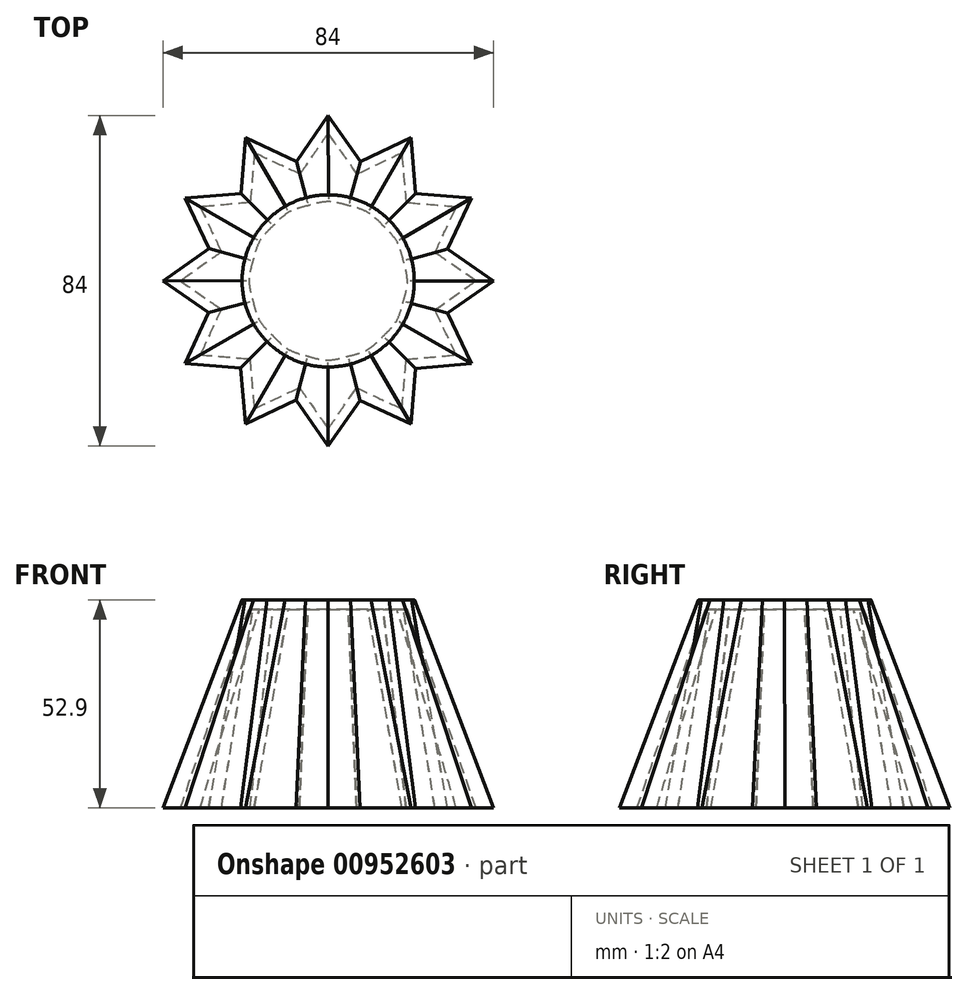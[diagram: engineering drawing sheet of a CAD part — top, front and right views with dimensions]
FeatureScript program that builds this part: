
annotation { "Feature Type Name" : "Feature", "Feature Type Description" : "" }
export const myFeature = defineFeature(function(context is Context, id is Id, definition is map)
    precondition{}
    {
        {
            var Q0;
            Q0=qCreatedBy(makeId("Top.planeOp"),FACE);
            cPlane(context, id + "F0", {"entities" : qUnion([Q0]), "cplaneType" : CPlaneType.OFFSET, "offset" : 47 * mm, "width" : 150 * mm, "height" : 150 * mm});
        }
        {
            var Q0;
            Q0=qCreatedBy(id+"F0.planeOp",FACE);
            var sketch = newSketch(context, id + "F1", { "sketchPlane" : qUnion([Q0])});
            skLineSegment(sketch, "E0", {"start": v(-9.31, 28.52) * mm, "end": v(0, 42) * mm});
            skLineSegment(sketch, "E1", {"start": v(0, 42) * mm, "end": v(9.47, 28.47) * mm});
            skLineSegment(sketch, "E2.1.0", {"start": v(-22.33, 20.04) * mm, "end": v(-21, 36.37) * mm});
            skLineSegment(sketch, "E2.2.0", {"start": v(-29.35, 6.2) * mm, "end": v(-36.37, 21) * mm});
            skLineSegment(sketch, "E2.3.0", {"start": v(-28.52, -9.31) * mm, "end": v(-42, 0) * mm});
            skLineSegment(sketch, "E2.4.0", {"start": v(-20.04, -22.33) * mm, "end": v(-36.37, -21) * mm});
            skLineSegment(sketch, "E2.5.0", {"start": v(-6.2, -29.35) * mm, "end": v(-21, -36.37) * mm});
            skLineSegment(sketch, "E2.6.0", {"start": v(9.31, -28.52) * mm, "end": v(0, -42) * mm});
            skLineSegment(sketch, "E2.7.0", {"start": v(22.33, -20.04) * mm, "end": v(21, -36.37) * mm});
            skLineSegment(sketch, "E2.8.0", {"start": v(29.35, -6.2) * mm, "end": v(36.37, -21) * mm});
            skLineSegment(sketch, "E2.9.0", {"start": v(28.52, 9.31) * mm, "end": v(42, 0) * mm});
            skLineSegment(sketch, "E2.10.0", {"start": v(20.04, 22.33) * mm, "end": v(36.37, 21) * mm});
            skLineSegment(sketch, "E2.11.0", {"start": v(6.2, 29.35) * mm, "end": v(21, 36.37) * mm});
            skPoint(sketch, "E2.center", {"position": v(0, 0) * mm});
            skLineSegment(sketch, "E3.1.0", {"start": v(-21, 36.37) * mm, "end": v(-6.03, 29.39) * mm});
            skLineSegment(sketch, "E3.2.0", {"start": v(-36.37, 21) * mm, "end": v(-19.92, 22.44) * mm});
            skLineSegment(sketch, "E3.3.0", {"start": v(-42, 0) * mm, "end": v(-28.47, 9.47) * mm});
            skLineSegment(sketch, "E3.4.0", {"start": v(-36.37, -21) * mm, "end": v(-29.39, -6.03) * mm});
            skLineSegment(sketch, "E3.5.0", {"start": v(-21, -36.37) * mm, "end": v(-22.44, -19.92) * mm});
            skLineSegment(sketch, "E3.6.0", {"start": v(0, -42) * mm, "end": v(-9.47, -28.47) * mm});
            skLineSegment(sketch, "E3.7.0", {"start": v(21, -36.37) * mm, "end": v(6.03, -29.39) * mm});
            skLineSegment(sketch, "E3.8.0", {"start": v(36.37, -21) * mm, "end": v(19.92, -22.44) * mm});
            skLineSegment(sketch, "E3.9.0", {"start": v(42, 0) * mm, "end": v(28.47, -9.47) * mm});
            skLineSegment(sketch, "E3.10.0", {"start": v(36.37, 21) * mm, "end": v(29.39, 6.03) * mm});
            skLineSegment(sketch, "E3.11.0", {"start": v(21, 36.37) * mm, "end": v(22.44, 19.92) * mm});
            skLineSegment(sketch, "E4", {"start": v(0, 42) * mm, "end": v(0, 30) * mm});
            skSolve(sketch);
        }
        {
            var Q0;
            Q0=qCreatedBy(id+"F0.planeOp",FACE);
            cPlane(context, id + "F2", {"entities" : qUnion([Q0]), "cplaneType" : CPlaneType.OFFSET, "offset" : 52.9 * mm, "width" : 150 * mm, "height" : 150 * mm});
        }
        {
            var Q0;
            Q0=qCreatedBy(id+"F2.planeOp",FACE);
            var sketch = newSketch(context, id + "F3", { "sketchPlane" : qUnion([Q0])});
            skCircle(sketch, "E5", {"center": v(0, 0) * mm, "radius": 21.87 * mm});
            skSolve(sketch);
        }
        {
            var Q0;
            Q0 = qSketchRegion(id + "F1", true);
            var Q1;
            Q1 = qSketchRegion(id + "F3", true);
            loft(context, id + "F4", {"sheetProfilesArray" : [{ "sheetProfileEntities" : qUnion([Q0]) }, { "sheetProfileEntities" : qUnion([Q1]) }]});
        }
        {
            var Q0;
            {var subQ35=sQuery(id+"F1.wireOp",EDGE,"E0");var subQ40=sQuery(id+"F1.wireOp",EDGE,"E1");var subQ47=makeQuery(id+"F1.imprint","INTERSECT",VERTEX,{"derivedFrom":[subQ35,subQ40]});Q0=makeQuery(id+"F4.opLoft","CAP_FACE",FACE,{"disambiguationData":[OSD([makeQuery(id+"F1.imprint","IMPRINT",FACE,{"disambiguationData":[TD([[makeQuery(id+"F1.imprint","IMPRINT",EDGE,{"disambiguationData":[TD([[subQ47,1.0]])],"derivedFrom":subQ35}),-1.0]])]})])],"isStart":true});}
            shell(context, id + "F5", {"entities" : qUnion([Q0]), "thickness" : 2.5 * mm});
        }
    });
